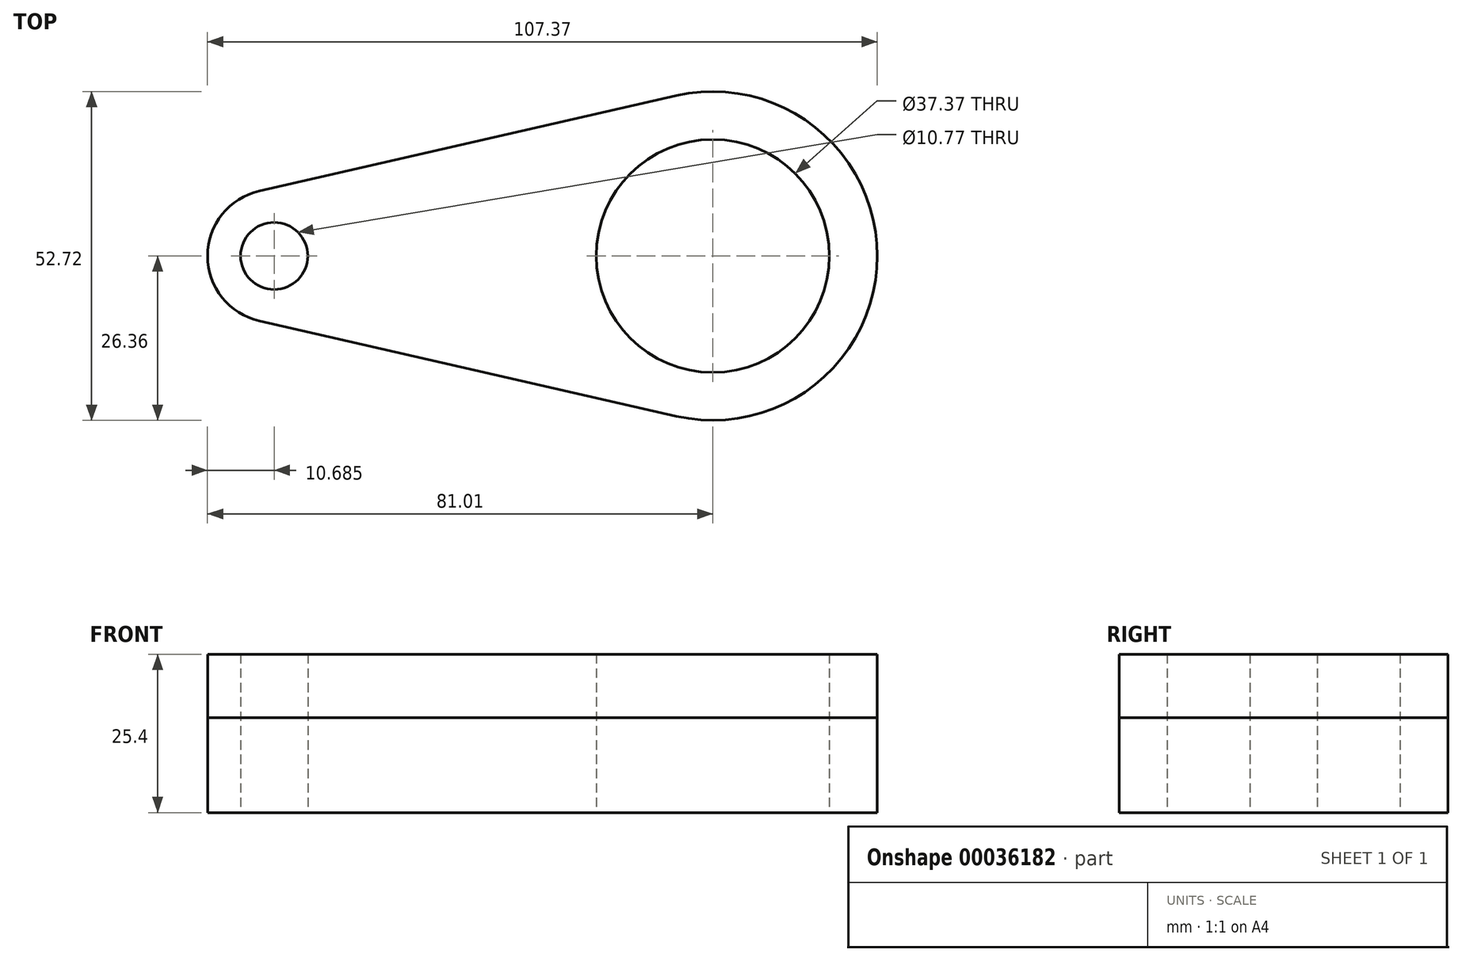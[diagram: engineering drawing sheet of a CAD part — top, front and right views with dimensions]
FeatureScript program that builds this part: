
annotation { "Feature Type Name" : "Feature", "Feature Type Description" : "" }
export const myFeature = defineFeature(function(context is Context, id is Id, definition is map)
    precondition{}
    {
        {
            var Q0;
            Q0=qCreatedBy(makeId("Top.planeOp"),FACE);
            var sketch = newSketch(context, id + "F0", { "sketchPlane" : qUnion([Q0])});
            skCircle(sketch, "E0", {"center": v(0, 0) * mm, "radius": 26.36 * mm});
            skCircle(sketch, "E1", {"center": v(-70.32, 0) * mm, "radius": 10.68 * mm});
            skLineSegment(sketch, "E2", {"start": v(-72.7, -10.42) * mm, "end": v(-5.87, -25.7) * mm});
            skLineSegment(sketch, "E3", {"start": v(-72.7, 10.42) * mm, "end": v(-5.87, 25.7) * mm});
            skCircle(sketch, "E4", {"center": v(-70.32, 0) * mm, "radius": 5.38 * mm});
            skCircle(sketch, "E5", {"center": v(0, 0) * mm, "radius": 18.69 * mm});
            skSolve(sketch);
        }
        {
            var Q0;
            Q0=makeQuery(id+"F0.imprint","IMPRINT",FACE,{"disambiguationData":[TD([[makeQuery(id+"F0.imprint","IMPRINT",EDGE,{"derivedFrom":sQuery(id+"F0.wireOp",EDGE,"E5")}),-1.0]])]});
            var Q1;
            {var subQ0=sQuery(id+"F0.wireOp",EDGE,"E2");Q1=makeQuery(id+"F0.imprint","IMPRINT",FACE,{"disambiguationData":[TD([[makeQuery(id+"F0.imprint","IMPRINT",EDGE,{"derivedFrom":subQ0}),1.0]])]});}
            var Q2;
            Q2=makeQuery(id+"F0.imprint","IMPRINT",FACE,{"disambiguationData":[TD([[makeQuery(id+"F0.imprint","IMPRINT",EDGE,{"derivedFrom":sQuery(id+"F0.wireOp",EDGE,"E4")}),-1.0]])]});
            extrude(context, id + "F1", {"entities" : qUnion([Q0, Q1, Q2]), "depth" : 25.4 * mm});
        }
        {
            var Q0;
            Q0=makeQuery(id+"F0.imprint","IMPRINT",FACE,{"disambiguationData":[TD([[makeQuery(id+"F0.imprint","IMPRINT",EDGE,{"derivedFrom":sQuery(id+"F0.wireOp",EDGE,"E4")}),1.0]])]});
            var Q1;
            Q1=makeQuery(id+"F0.imprint","IMPRINT",FACE,{"disambiguationData":[TD([[makeQuery(id+"F0.imprint","IMPRINT",EDGE,{"derivedFrom":sQuery(id+"F0.wireOp",EDGE,"E5")}),1.0]])]});
            var Q2;
            Q2=makeQuery(id+"F0.imprint","IMPRINT",FACE,{"disambiguationData":[TD([[makeQuery(id+"F0.imprint","IMPRINT",EDGE,{"derivedFrom":sQuery(id+"F0.wireOp",EDGE,"E4")}),-1.0]])]});
            var Q3;
            Q3=makeQuery(id+"F0.imprint","IMPRINT",FACE,{"disambiguationData":[TD([[makeQuery(id+"F0.imprint","IMPRINT",EDGE,{"derivedFrom":sQuery(id+"F0.wireOp",EDGE,"E5")}),-1.0]])]});
            var Q4;
            {var subQ1=sQuery(id+"F0.wireOp",EDGE,"E2");Q4=makeQuery(id+"F0.imprint","IMPRINT",FACE,{"disambiguationData":[TD([[makeQuery(id+"F0.imprint","IMPRINT",EDGE,{"derivedFrom":subQ1}),1.0]])]});}
            extrude(context, id + "F2", {"entities" : qUnion([Q0, Q1, Q2, Q3, Q4]), "depth" : 15.22 * mm});
        }
    });
